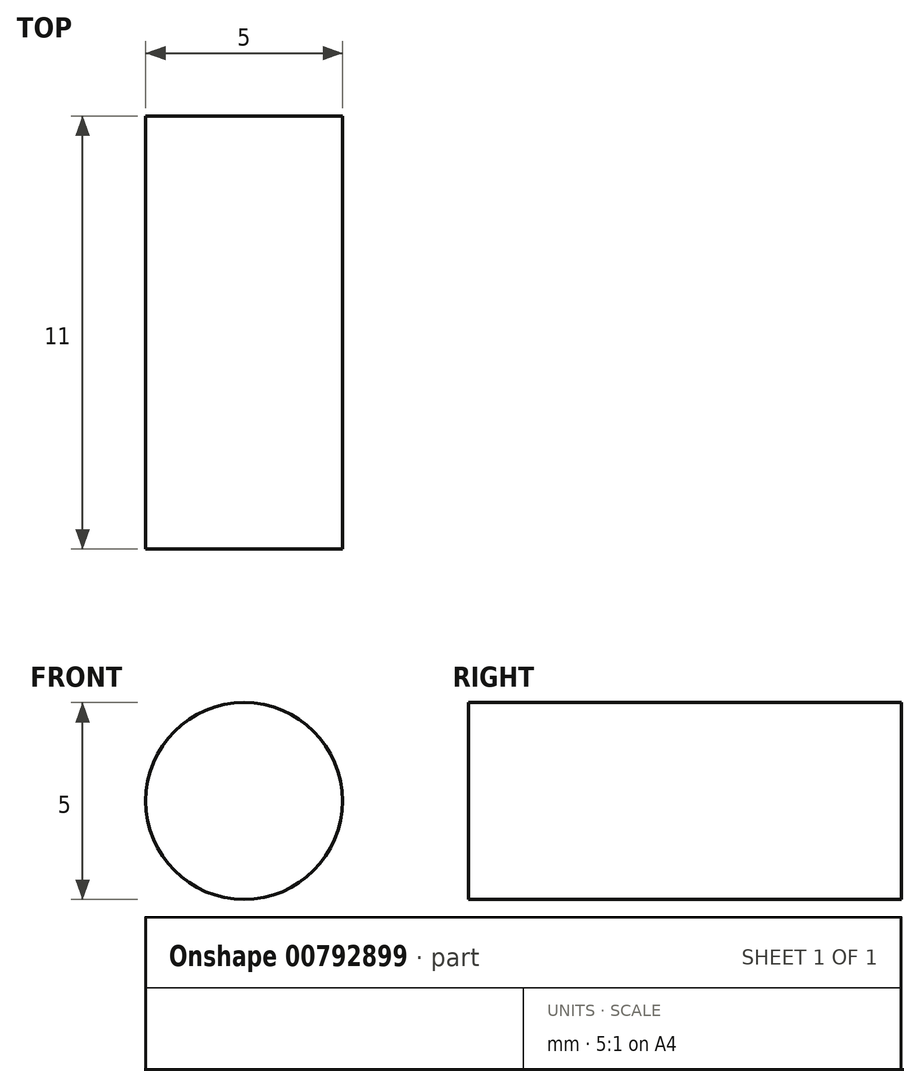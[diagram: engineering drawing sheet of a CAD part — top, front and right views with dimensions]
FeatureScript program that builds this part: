
annotation { "Feature Type Name" : "Feature", "Feature Type Description" : "" }
export const myFeature = defineFeature(function(context is Context, id is Id, definition is map)
    precondition{}
    {
        {
            var Q0;
            Q0=qCreatedBy(makeId("Front.planeOp"),FACE);
            var sketch = newSketch(context, id + "F0", { "sketchPlane" : qUnion([Q0])});
            skCircle(sketch, "E0", {"center": v(0, 0) * mm, "radius": 2.5 * mm});
            skSolve(sketch);
        }
        {
            var Q0;
            Q0=makeQuery(id+"F0.imprint","IMPRINT",FACE,{"disambiguationData":[TD([[makeQuery(id+"F0.imprint","IMPRINT",EDGE,{"derivedFrom":sQuery(id+"F0.wireOp",EDGE,"E0")}),1.0]])]});
            extrude(context, id + "F1", {"entities" : qUnion([Q0]), "depth" : 11 * mm, "offsetDistance" : 25 * mm});
        }
    });
